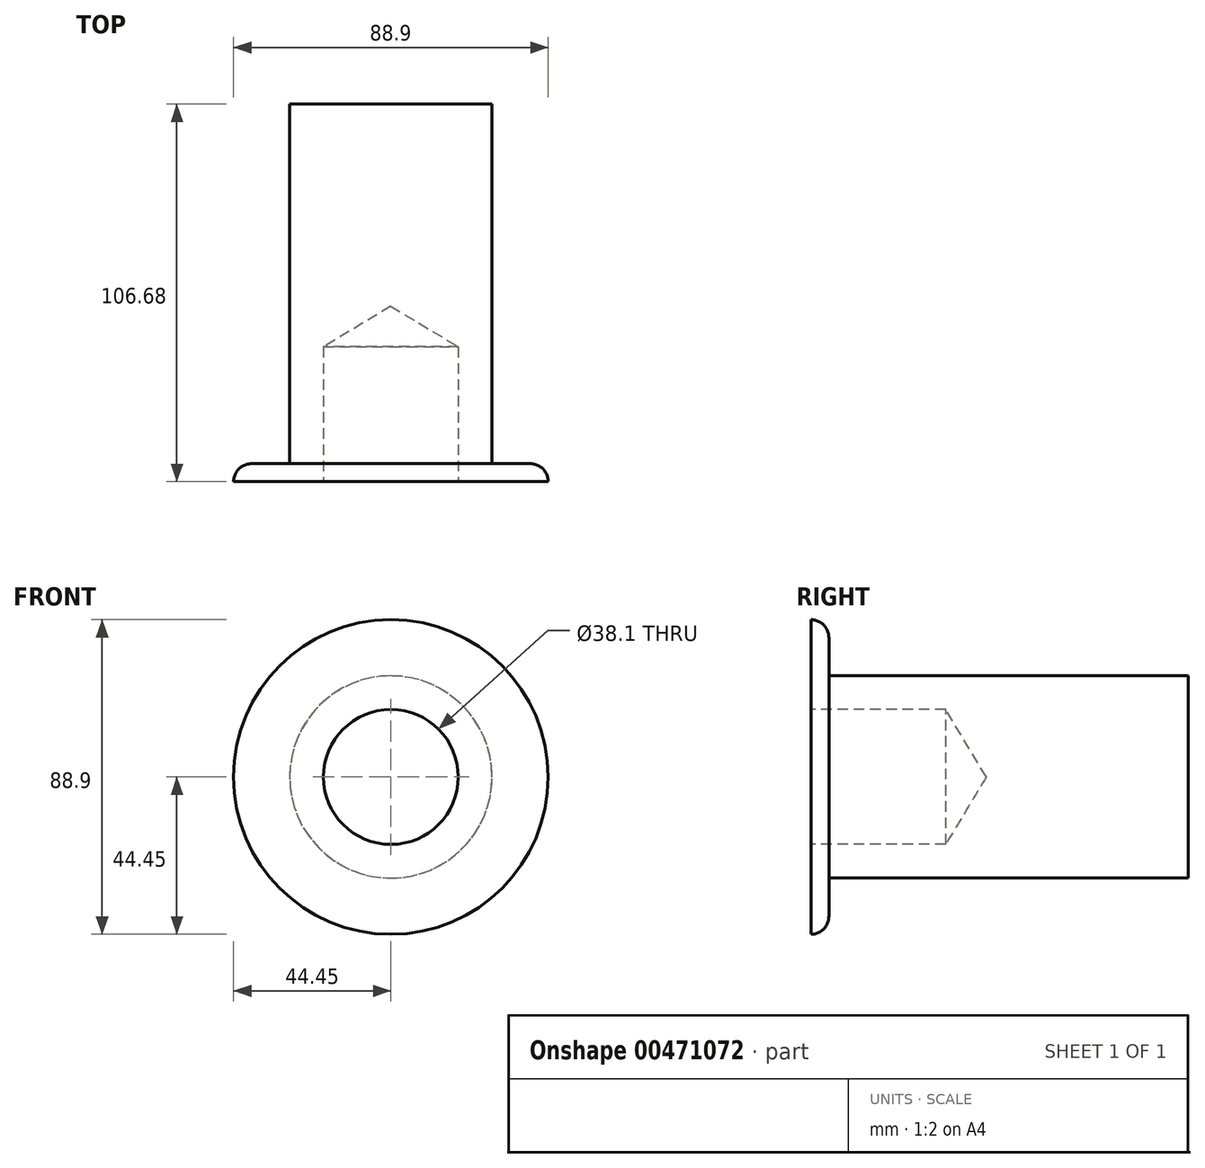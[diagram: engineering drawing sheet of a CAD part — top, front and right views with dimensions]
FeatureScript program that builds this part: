
annotation { "Feature Type Name" : "Feature", "Feature Type Description" : "" }
export const myFeature = defineFeature(function(context is Context, id is Id, definition is map)
    precondition{}
    {
        {
            var Q0;
            Q0=qCreatedBy(makeId("Front.planeOp"),FACE);
            var sketch = newSketch(context, id + "F0", { "sketchPlane" : qUnion([Q0])});
            skCircle(sketch, "E0", {"center": v(0, 0) * mm, "radius": 44.45 * mm});
            skSolve(sketch);
        }
        {
            var Q0;
            Q0=makeQuery(id+"F0.imprint","IMPRINT",FACE,{"disambiguationData":[TD([[makeQuery(id+"F0.imprint","IMPRINT",EDGE,{"derivedFrom":sQuery(id+"F0.wireOp",EDGE,"E0")}),1.0]])]});
            extrude(context, id + "F1", {"entities" : qUnion([Q0]), "depth" : 5.08 * mm});
        }
        {
            var Q0;
            Q0=makeQuery(id+"F1.opExtrude","CAP_EDGE",EDGE,{"disambiguationData":[OSD([sQuery(id+"F0.wireOp",EDGE,"E0")])],"isStart":true});
            fillet(context, id + "F2", {"entities" : qUnion([Q0]), "radius" : 5.08 * mm, "tangentPropagation" : true, "allowEdgeOverflow" : false});
        }
        {
            var Q0;
            Q0=makeQuery(id+"F1.opExtrude","CAP_FACE",FACE,{"disambiguationData":[OSD([sQuery(id+"F0.wireOp",EDGE,"E0")])],"isStart":false});
            var sketch = newSketch(context, id + "F3", { "sketchPlane" : qUnion([Q0])});
            skCircle(sketch, "E1", {"center": v(0, 0) * mm, "radius": 19.05 * mm});
            skSolve(sketch);
        }
        {
            var Q0;
            Q0=makeQuery(id+"F1.opExtrude","CAP_FACE",FACE,{"disambiguationData":[OSD([sQuery(id+"F0.wireOp",EDGE,"E0")])],"isStart":true});
            var sketch = newSketch(context, id + "F4", { "sketchPlane" : qUnion([Q0])});
            skCircle(sketch, "E2", {"center": v(0, 0) * mm, "radius": 28.58 * mm});
            skSolve(sketch);
        }
        {
            var Q0;
            Q0=makeQuery(id+"F4.imprint","IMPRINT",FACE,{"disambiguationData":[TD([[makeQuery(id+"F4.imprint","IMPRINT",EDGE,{"derivedFrom":sQuery(id+"F4.wireOp",EDGE,"E2")}),1.0]])]});
            extrude(context, id + "F5", {"entities" : qUnion([Q0]), "operationType" : NewBodyOperationType.ADD, "depth" : 101.6 * mm});
        }
        {
            var Q0;
            Q0=sQuery(id+"F3.wireOp",VERTEX,"E1.center");
            var Q1;
            Q1=makeQuery(id+"F1.opExtrude","SWEPT_BODY",BODY,{"disambiguationData":[OSD([sQuery(id+"F0.wireOp",EDGE,"E0")])]});
            hole(context, id + "F6", {"style" : HoleStyle.SIMPLE, "endStyle" : HoleEndStyle.BLIND, "holeDiameter" : 38.1 * mm, "holeDepth" : 38.1 * mm, "isTappedThrough" : true, "tappedDepth" : 12.7 * mm, "tapClearance" : 3, "locations" : qUnion([Q0]), "scope" : qUnion([Q1])});
        }
    });
